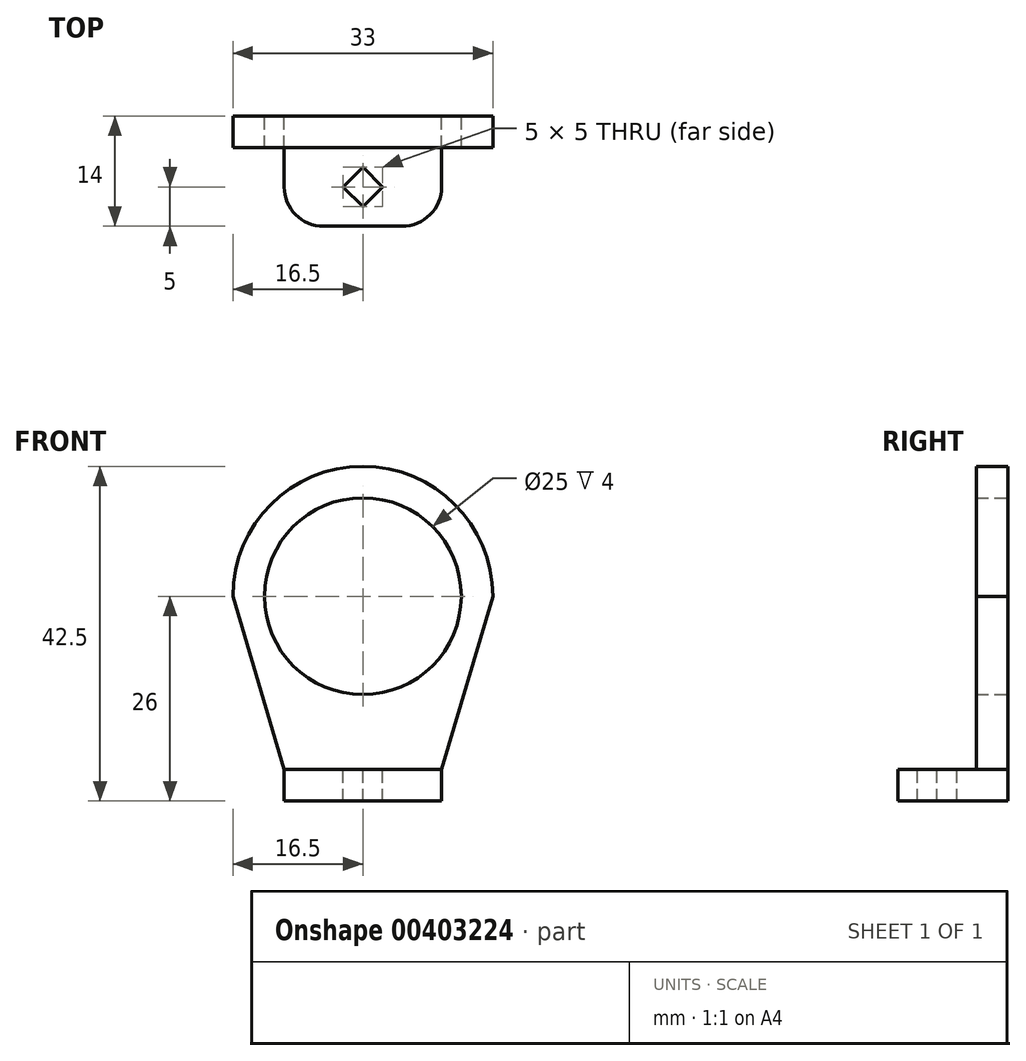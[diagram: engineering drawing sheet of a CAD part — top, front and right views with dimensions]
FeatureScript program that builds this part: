
annotation { "Feature Type Name" : "Feature", "Feature Type Description" : "" }
export const myFeature = defineFeature(function(context is Context, id is Id, definition is map)
    precondition{}
    {
        {
            var Q0;
            Q0=qCreatedBy(makeId("Front.planeOp"),FACE);
            var sketch = newSketch(context, id + "F0", { "sketchPlane" : qUnion([Q0])});
            skLineSegment(sketch, "E0", {"start": v(0, 0) * mm, "end": v(-10, 0) * mm});
            skLineSegment(sketch, "E1.bottom", {"start": v(-10, 0) * mm, "end": v(10, 0) * mm});
            skLineSegment(sketch, "E1.top", {"start": v(-10, 4) * mm, "end": v(10, 4) * mm});
            skLineSegment(sketch, "E1.left", {"start": v(-10, 0) * mm, "end": v(-10, 4) * mm});
            skLineSegment(sketch, "E1.right", {"start": v(10, 0) * mm, "end": v(10, 4) * mm});
            skCircle(sketch, "E2", {"center": v(0, 26) * mm, "radius": 12.5 * mm});
            skArc(sketch, "E3", {"start": v(-16.5, 26) * mm, "mid": v(0, 42.5) * mm, "end": v(16.5, 26) * mm});
            skLineSegment(sketch, "E4", {"start": v(-16.5, 26) * mm, "end": v(-10, 4) * mm});
            skLineSegment(sketch, "E5", {"start": v(16.5, 26) * mm, "end": v(10, 4) * mm});
            skSolve(sketch);
        }
        {
            var Q0;
            Q0=makeQuery(id+"F0.imprint","IMPRINT",FACE,{"disambiguationData":[TD([[makeQuery(id+"F0.imprint","IMPRINT",EDGE,{"derivedFrom":sQuery(id+"F0.wireOp",EDGE,"E1.top")}),-1.0]])]});
            extrude(context, id + "F1", {"entities" : qUnion([Q0]), "depth" : 14 * mm});
        }
        {
            var Q0;
            Q0=makeQuery(id+"F0.imprint","IMPRINT",FACE,{"disambiguationData":[TD([[makeQuery(id+"F0.imprint","IMPRINT",EDGE,{"derivedFrom":sQuery(id+"F0.wireOp",EDGE,"E1.top")}),1.0]])]});
            extrude(context, id + "F2", {"entities" : qUnion([Q0]), "operationType" : NewBodyOperationType.ADD, "depth" : 4 * mm});
        }
        {
            var Q0;
            Q0=makeQuery(id+"F1.opExtrude","CAP_EDGE",EDGE,{"disambiguationData":[OSD([sQuery(id+"F0.wireOp",EDGE,"E1.left")])],"isStart":false});
            var Q1;
            Q1=makeQuery(id+"F1.opExtrude","CAP_EDGE",EDGE,{"disambiguationData":[OSD([sQuery(id+"F0.wireOp",EDGE,"E1.right")])],"isStart":false});
            fillet(context, id + "F3", {"entities" : qUnion([Q0, Q1]), "radius" : 5 * mm, "tangentPropagation" : true, "allowEdgeOverflow" : false});
        }
        {
            var Q0;
            Q0=makeQuery(id+"F1.opExtrude","SWEPT_FACE",FACE,{"disambiguationData":[OSD([sQuery(id+"F0.wireOp",EDGE,"E1.top")])]});
            var sketch = newSketch(context, id + "F4", { "sketchPlane" : qUnion([Q0])});
            skLineSegment(sketch, "E6", {"start": v(0, -9) * mm, "end": v(0, -6.5) * mm});
            skLineSegment(sketch, "E7", {"start": v(0, -9) * mm, "end": v(-2.5, -9) * mm});
            skLineSegment(sketch, "E8", {"start": v(0, -9) * mm, "end": v(0, -11.5) * mm});
            skLineSegment(sketch, "E9", {"start": v(0, -9) * mm, "end": v(2.5, -9) * mm});
            skLineSegment(sketch, "E10", {"start": v(2.5, -9) * mm, "end": v(0, -6.5) * mm});
            skLineSegment(sketch, "E11", {"start": v(0, -6.5) * mm, "end": v(-2.5, -9) * mm});
            skLineSegment(sketch, "E12", {"start": v(-2.5, -9) * mm, "end": v(0, -11.5) * mm});
            skLineSegment(sketch, "E13", {"start": v(0, -11.5) * mm, "end": v(2.5, -9) * mm});
            skSolve(sketch);
        }
        {
            var Q0;
            Q0=makeQuery(id+"F4.imprint","IMPRINT",FACE,{"disambiguationData":[TD([[makeQuery(id+"F4.imprint","IMPRINT",EDGE,{"derivedFrom":sQuery(id+"F4.wireOp",EDGE,"E6")}),1.0]])]});
            var Q1;
            Q1=makeQuery(id+"F4.imprint","IMPRINT",FACE,{"disambiguationData":[TD([[makeQuery(id+"F4.imprint","IMPRINT",EDGE,{"derivedFrom":sQuery(id+"F4.wireOp",EDGE,"E6")}),-1.0]])]});
            var Q2;
            Q2=makeQuery(id+"F4.imprint","IMPRINT",FACE,{"disambiguationData":[TD([[makeQuery(id+"F4.imprint","IMPRINT",EDGE,{"derivedFrom":sQuery(id+"F4.wireOp",EDGE,"E8")}),1.0]])]});
            var Q3;
            Q3=makeQuery(id+"F4.imprint","IMPRINT",FACE,{"disambiguationData":[TD([[makeQuery(id+"F4.imprint","IMPRINT",EDGE,{"derivedFrom":sQuery(id+"F4.wireOp",EDGE,"E7")}),1.0]])]});
            extrude(context, id + "F5", {"entities" : qUnion([Q0, Q1, Q2, Q3]), "operationType" : NewBodyOperationType.REMOVE, "oppositeDirection" : true, "depth" : 4 * mm});
        }
    });
